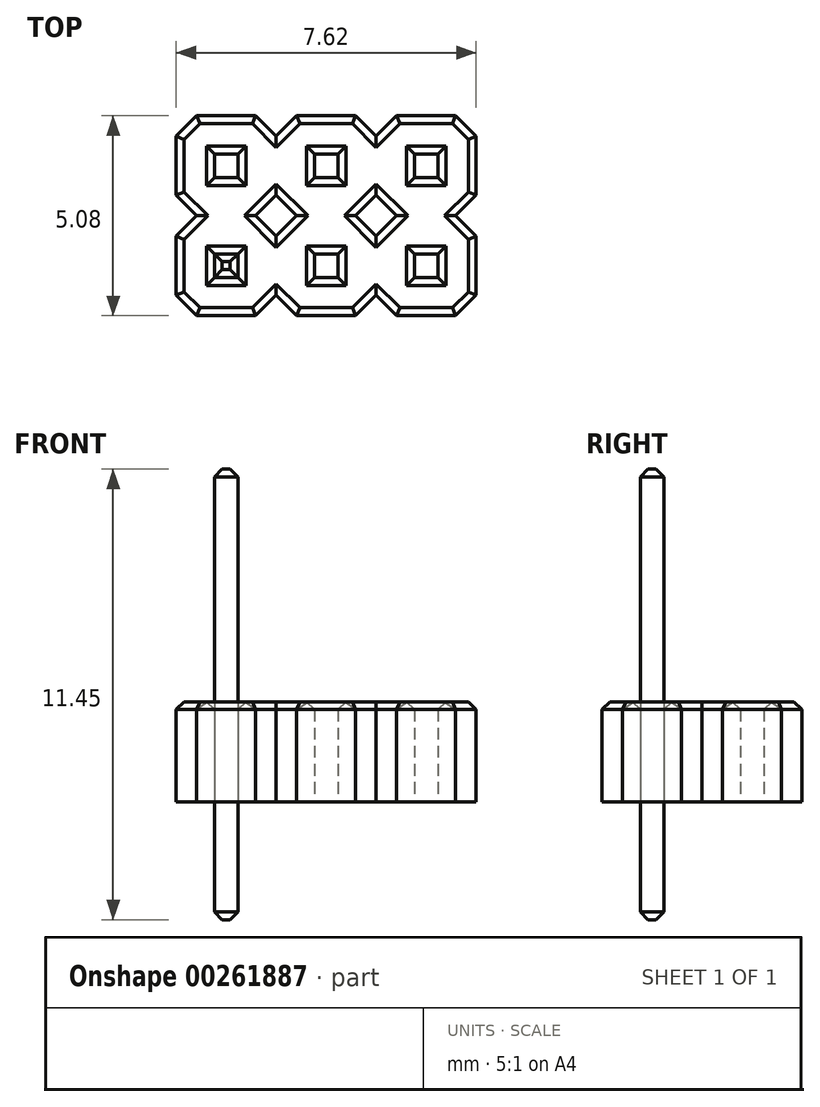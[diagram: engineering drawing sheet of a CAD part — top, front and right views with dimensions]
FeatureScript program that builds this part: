
annotation { "Feature Type Name" : "Feature", "Feature Type Description" : "" }
export const myFeature = defineFeature(function(context is Context, id is Id, definition is map)
    precondition{}
    {
        {
            var Q0;
            Q0=qCreatedBy(makeId("Top.planeOp"),FACE);
            var sketch = newSketch(context, id + "F0", { "sketchPlane" : qUnion([Q0])});
            skLineSegment(sketch, "E0.bottom", {"start": v(0.3, -0.3) * mm, "end": v(-0.3, -0.3) * mm});
            skLineSegment(sketch, "E0.top", {"start": v(0.3, 0.3) * mm, "end": v(-0.3, 0.3) * mm});
            skLineSegment(sketch, "E0.left", {"start": v(0.3, -0.3) * mm, "end": v(0.3, 0.3) * mm});
            skLineSegment(sketch, "E0.right", {"start": v(-0.3, -0.3) * mm, "end": v(-0.3, 0.3) * mm});
            skPoint(sketch, "E0.middle", {"position": v(0, 0) * mm});
            skLineSegment(sketch, "E1.0.1.0", {"start": v(0.3, 2.84) * mm, "end": v(-0.3, 2.84) * mm});
            skLineSegment(sketch, "E1.0.1.1", {"start": v(-0.3, 2.24) * mm, "end": v(-0.3, 2.84) * mm});
            skLineSegment(sketch, "E1.0.1.2", {"start": v(0.3, 2.24) * mm, "end": v(-0.3, 2.24) * mm});
            skLineSegment(sketch, "E1.0.1.3", {"start": v(0.3, 2.24) * mm, "end": v(0.3, 2.84) * mm});
            skLineSegment(sketch, "E1.1.0.0", {"start": v(2.84, 0.3) * mm, "end": v(2.24, 0.3) * mm});
            skLineSegment(sketch, "E1.1.0.1", {"start": v(2.24, -0.3) * mm, "end": v(2.24, 0.3) * mm});
            skLineSegment(sketch, "E1.1.0.2", {"start": v(2.84, -0.3) * mm, "end": v(2.24, -0.3) * mm});
            skLineSegment(sketch, "E1.1.0.3", {"start": v(2.84, -0.3) * mm, "end": v(2.84, 0.3) * mm});
            skLineSegment(sketch, "E1.1.1.0", {"start": v(2.84, 2.84) * mm, "end": v(2.24, 2.84) * mm});
            skLineSegment(sketch, "E1.1.1.1", {"start": v(2.24, 2.24) * mm, "end": v(2.24, 2.84) * mm});
            skLineSegment(sketch, "E1.1.1.2", {"start": v(2.84, 2.24) * mm, "end": v(2.24, 2.24) * mm});
            skLineSegment(sketch, "E1.1.1.3", {"start": v(2.84, 2.24) * mm, "end": v(2.84, 2.84) * mm});
            skLineSegment(sketch, "E1.2.0.0", {"start": v(5.38, 0.3) * mm, "end": v(4.78, 0.3) * mm});
            skLineSegment(sketch, "E1.2.0.1", {"start": v(4.78, -0.3) * mm, "end": v(4.78, 0.3) * mm});
            skLineSegment(sketch, "E1.2.0.2", {"start": v(5.38, -0.3) * mm, "end": v(4.78, -0.3) * mm});
            skLineSegment(sketch, "E1.2.0.3", {"start": v(5.38, -0.3) * mm, "end": v(5.38, 0.3) * mm});
            skLineSegment(sketch, "E1.2.1.0", {"start": v(5.38, 2.84) * mm, "end": v(4.78, 2.84) * mm});
            skLineSegment(sketch, "E1.2.1.1", {"start": v(4.78, 2.24) * mm, "end": v(4.78, 2.84) * mm});
            skLineSegment(sketch, "E1.2.1.2", {"start": v(5.38, 2.24) * mm, "end": v(4.78, 2.24) * mm});
            skLineSegment(sketch, "E1.2.1.3", {"start": v(5.38, 2.24) * mm, "end": v(5.38, 2.84) * mm});
            skLineSegment(sketch, "E1.direction1", {"start": v(-0.3, 0.3) * mm, "end": v(2.24, 0.3) * mm, "construction": true});
            skLineSegment(sketch, "E1.direction2", {"start": v(-0.3, 0.3) * mm, "end": v(-0.3, 2.84) * mm, "construction": true});
            skSolve(sketch);
        }
        {
            var Q0;
            Q0=qCreatedBy(makeId("Top.planeOp"),FACE);
            cPlane(context, id + "F1", {"entities" : qUnion([Q0]), "cplaneType" : CPlaneType.OFFSET, "offset" : 3 * mm, "width" : 150 * mm, "height" : 150 * mm});
        }
        {
            var Q0;
            Q0=qCreatedBy(id+"F1.planeOp",FACE);
            var sketch = newSketch(context, id + "F2", { "sketchPlane" : qUnion([Q0])});
            skLineSegment(sketch, "E2.bottom", {"start": v(0.75, 1.27) * mm, "end": v(-0.75, 1.27) * mm});
            skLineSegment(sketch, "E2.top", {"start": v(0.75, -1.27) * mm, "end": v(-0.75, -1.27) * mm});
            skLineSegment(sketch, "E2.left", {"start": v(1.27, 0.75) * mm, "end": v(1.27, -0.75) * mm});
            skLineSegment(sketch, "E2.right", {"start": v(-1.27, 0.75) * mm, "end": v(-1.27, -0.75) * mm});
            skPoint(sketch, "E2.middle", {"position": v(0, 0) * mm});
            skLineSegment(sketch, "E3", {"start": v(-1.27, 0.75) * mm, "end": v(-0.75, 1.27) * mm});
            skLineSegment(sketch, "E4", {"start": v(1.27, 0.75) * mm, "end": v(0.75, 1.27) * mm});
            skLineSegment(sketch, "E5", {"start": v(-1.27, -0.75) * mm, "end": v(-0.75, -1.27) * mm});
            skLineSegment(sketch, "E6", {"start": v(0.75, -1.27) * mm, "end": v(1.27, -0.75) * mm});
            skPoint(sketch, "E7.orphan", {"position": v(1.27, 1.27) * mm});
            skPoint(sketch, "E8.orphan", {"position": v(-1.27, 1.27) * mm});
            skPoint(sketch, "E9.orphan", {"position": v(-1.27, -1.27) * mm});
            skPoint(sketch, "E10.orphan", {"position": v(1.27, -1.27) * mm});
            skLineSegment(sketch, "E11.0.1.1", {"start": v(0.75, 1.27) * mm, "end": v(1.27, 1.8) * mm});
            skLineSegment(sketch, "E11.0.1.2", {"start": v(1.27, 3.29) * mm, "end": v(1.27, 1.8) * mm});
            skLineSegment(sketch, "E11.0.1.3", {"start": v(1.27, 3.29) * mm, "end": v(0.75, 3.8) * mm});
            skLineSegment(sketch, "E11.0.1.4", {"start": v(0.75, 3.81) * mm, "end": v(-0.75, 3.81) * mm});
            skLineSegment(sketch, "E11.0.1.5", {"start": v(-1.27, 3.29) * mm, "end": v(-0.75, 3.8) * mm});
            skLineSegment(sketch, "E11.0.1.6", {"start": v(-1.27, 3.29) * mm, "end": v(-1.27, 1.8) * mm});
            skLineSegment(sketch, "E11.0.1.7", {"start": v(-1.27, 1.8) * mm, "end": v(-0.75, 1.27) * mm});
            skLineSegment(sketch, "E11.1.0.0", {"start": v(3.29, -1.27) * mm, "end": v(1.8, -1.27) * mm});
            skLineSegment(sketch, "E11.1.0.1", {"start": v(3.29, -1.27) * mm, "end": v(3.8, -0.75) * mm});
            skLineSegment(sketch, "E11.1.0.2", {"start": v(3.81, 0.75) * mm, "end": v(3.81, -0.75) * mm});
            skLineSegment(sketch, "E11.1.0.3", {"start": v(3.81, 0.75) * mm, "end": v(3.29, 1.27) * mm});
            skLineSegment(sketch, "E11.1.0.4", {"start": v(3.29, 1.27) * mm, "end": v(1.8, 1.27) * mm});
            skLineSegment(sketch, "E11.1.0.5", {"start": v(1.27, 0.75) * mm, "end": v(1.8, 1.27) * mm});
            skLineSegment(sketch, "E11.1.0.7", {"start": v(1.27, -0.75) * mm, "end": v(1.8, -1.27) * mm});
            skLineSegment(sketch, "E11.1.1.0", {"start": v(3.29, 1.27) * mm, "end": v(1.8, 1.27) * mm});
            skLineSegment(sketch, "E11.1.1.1", {"start": v(3.29, 1.27) * mm, "end": v(3.8, 1.8) * mm});
            skLineSegment(sketch, "E11.1.1.2", {"start": v(3.81, 3.29) * mm, "end": v(3.81, 1.8) * mm});
            skLineSegment(sketch, "E11.1.1.3", {"start": v(3.81, 3.29) * mm, "end": v(3.29, 3.8) * mm});
            skLineSegment(sketch, "E11.1.1.4", {"start": v(3.29, 3.81) * mm, "end": v(1.8, 3.81) * mm});
            skLineSegment(sketch, "E11.1.1.5", {"start": v(1.27, 3.29) * mm, "end": v(1.8, 3.8) * mm});
            skLineSegment(sketch, "E11.1.1.6", {"start": v(1.27, 3.29) * mm, "end": v(1.27, 1.8) * mm});
            skLineSegment(sketch, "E11.1.1.7", {"start": v(1.27, 1.8) * mm, "end": v(1.8, 1.27) * mm});
            skLineSegment(sketch, "E11.2.0.0", {"start": v(5.83, -1.27) * mm, "end": v(4.33, -1.27) * mm});
            skLineSegment(sketch, "E11.2.0.1", {"start": v(5.83, -1.27) * mm, "end": v(6.35, -0.75) * mm});
            skLineSegment(sketch, "E11.2.0.2", {"start": v(6.35, 0.75) * mm, "end": v(6.35, -0.75) * mm});
            skLineSegment(sketch, "E11.2.0.3", {"start": v(6.35, 0.75) * mm, "end": v(5.83, 1.27) * mm});
            skLineSegment(sketch, "E11.2.0.4", {"start": v(5.83, 1.27) * mm, "end": v(4.33, 1.27) * mm});
            skLineSegment(sketch, "E11.2.0.5", {"start": v(3.8, 0.75) * mm, "end": v(4.33, 1.27) * mm});
            skLineSegment(sketch, "E11.2.0.6", {"start": v(3.81, 0.75) * mm, "end": v(3.81, -0.75) * mm});
            skLineSegment(sketch, "E11.2.0.7", {"start": v(3.8, -0.75) * mm, "end": v(4.33, -1.27) * mm});
            skLineSegment(sketch, "E11.2.1.0", {"start": v(5.83, 1.27) * mm, "end": v(4.33, 1.27) * mm});
            skLineSegment(sketch, "E11.2.1.1", {"start": v(5.83, 1.27) * mm, "end": v(6.35, 1.8) * mm});
            skLineSegment(sketch, "E11.2.1.2", {"start": v(6.35, 3.29) * mm, "end": v(6.35, 1.8) * mm});
            skLineSegment(sketch, "E11.2.1.3", {"start": v(6.35, 3.29) * mm, "end": v(5.83, 3.8) * mm});
            skLineSegment(sketch, "E11.2.1.4", {"start": v(5.83, 3.81) * mm, "end": v(4.33, 3.81) * mm});
            skLineSegment(sketch, "E11.2.1.5", {"start": v(3.8, 3.29) * mm, "end": v(4.33, 3.8) * mm});
            skLineSegment(sketch, "E11.2.1.6", {"start": v(3.81, 3.29) * mm, "end": v(3.81, 1.8) * mm});
            skLineSegment(sketch, "E11.2.1.7", {"start": v(3.8, 1.8) * mm, "end": v(4.33, 1.27) * mm});
            skLineSegment(sketch, "E11.direction1", {"start": v(-0.75, -1.27) * mm, "end": v(1.8, -1.27) * mm, "construction": true});
            skLineSegment(sketch, "E11.direction2", {"start": v(-0.75, -1.27) * mm, "end": v(-0.75, 1.27) * mm, "construction": true});
            skLineSegment(sketch, "E12.bottom", {"start": v(0.3, -0.3) * mm, "end": v(-0.3, -0.3) * mm});
            skLineSegment(sketch, "E12.top", {"start": v(0.3, 0.3) * mm, "end": v(-0.3, 0.3) * mm});
            skLineSegment(sketch, "E12.left", {"start": v(0.3, -0.3) * mm, "end": v(0.3, 0.3) * mm});
            skLineSegment(sketch, "E12.right", {"start": v(-0.3, -0.3) * mm, "end": v(-0.3, 0.3) * mm});
            skLineSegment(sketch, "E13.0.1.0", {"start": v(0.3, 2.84) * mm, "end": v(-0.3, 2.84) * mm});
            skLineSegment(sketch, "E13.0.1.1", {"start": v(0.3, 2.24) * mm, "end": v(0.3, 2.84) * mm});
            skLineSegment(sketch, "E13.0.1.2", {"start": v(0.3, 2.24) * mm, "end": v(-0.3, 2.24) * mm});
            skLineSegment(sketch, "E13.0.1.3", {"start": v(-0.3, 2.24) * mm, "end": v(-0.3, 2.84) * mm});
            skLineSegment(sketch, "E13.1.0.0", {"start": v(2.84, 0.3) * mm, "end": v(2.24, 0.3) * mm});
            skLineSegment(sketch, "E13.1.0.1", {"start": v(2.84, -0.3) * mm, "end": v(2.84, 0.3) * mm});
            skLineSegment(sketch, "E13.1.0.2", {"start": v(2.84, -0.3) * mm, "end": v(2.24, -0.3) * mm});
            skLineSegment(sketch, "E13.1.0.3", {"start": v(2.24, -0.3) * mm, "end": v(2.24, 0.3) * mm});
            skLineSegment(sketch, "E13.1.1.0", {"start": v(2.84, 2.84) * mm, "end": v(2.24, 2.84) * mm});
            skLineSegment(sketch, "E13.1.1.1", {"start": v(2.84, 2.24) * mm, "end": v(2.84, 2.84) * mm});
            skLineSegment(sketch, "E13.1.1.2", {"start": v(2.84, 2.24) * mm, "end": v(2.24, 2.24) * mm});
            skLineSegment(sketch, "E13.1.1.3", {"start": v(2.24, 2.24) * mm, "end": v(2.24, 2.84) * mm});
            skLineSegment(sketch, "E13.2.0.0", {"start": v(5.38, 0.3) * mm, "end": v(4.78, 0.3) * mm});
            skLineSegment(sketch, "E13.2.0.1", {"start": v(5.38, -0.3) * mm, "end": v(5.38, 0.3) * mm});
            skLineSegment(sketch, "E13.2.0.2", {"start": v(5.38, -0.3) * mm, "end": v(4.78, -0.3) * mm});
            skLineSegment(sketch, "E13.2.0.3", {"start": v(4.78, -0.3) * mm, "end": v(4.78, 0.3) * mm});
            skLineSegment(sketch, "E13.2.1.0", {"start": v(5.38, 2.84) * mm, "end": v(4.78, 2.84) * mm});
            skLineSegment(sketch, "E13.2.1.1", {"start": v(5.38, 2.24) * mm, "end": v(5.38, 2.84) * mm});
            skLineSegment(sketch, "E13.2.1.2", {"start": v(5.38, 2.24) * mm, "end": v(4.78, 2.24) * mm});
            skLineSegment(sketch, "E13.2.1.3", {"start": v(4.78, 2.24) * mm, "end": v(4.78, 2.84) * mm});
            skLineSegment(sketch, "E13.direction1", {"start": v(-0.3, 0.3) * mm, "end": v(2.24, 0.3) * mm, "construction": true});
            skLineSegment(sketch, "E13.direction2", {"start": v(-0.3, 0.3) * mm, "end": v(-0.3, 2.84) * mm, "construction": true});
            skSolve(sketch);
        }
        {
            var Q0;
            Q0 = qSketchRegion(id + "F2", true);
            extrude(context, id + "F3", {"entities" : qUnion([Q0]), "depth" : 2.54 * mm});
        }
        {
            var Q0;
            Q0 = qSketchRegion(id + "F0", true);
            extrude(context, id + "F4", {"entities" : qUnion([Q0]), "depth" : 11.45 * mm});
        }
        {
            var Q0;
            Q0=makeQuery(id+"F4.opExtrude","CAP_FACE",FACE,{"disambiguationData":[OSD([sQuery(id+"F0.wireOp",EDGE,"E1.0.1.0"),sQuery(id+"F0.wireOp",EDGE,"E1.0.1.1"),sQuery(id+"F0.wireOp",EDGE,"E1.0.1.2"),sQuery(id+"F0.wireOp",EDGE,"E1.0.1.3")])],"isStart":false});
            var Q1;
            Q1=makeQuery(id+"F4.opExtrude","CAP_FACE",FACE,{"disambiguationData":[OSD([sQuery(id+"F0.wireOp",EDGE,"E0.bottom"),sQuery(id+"F0.wireOp",EDGE,"E0.top"),sQuery(id+"F0.wireOp",EDGE,"E0.left"),sQuery(id+"F0.wireOp",EDGE,"E0.right")])],"isStart":false});
            var Q2;
            Q2=makeQuery(id+"F4.opExtrude","CAP_FACE",FACE,{"disambiguationData":[OSD([sQuery(id+"F0.wireOp",EDGE,"E1.1.1.0"),sQuery(id+"F0.wireOp",EDGE,"E1.1.1.1"),sQuery(id+"F0.wireOp",EDGE,"E1.1.1.2"),sQuery(id+"F0.wireOp",EDGE,"E1.1.1.3")])],"isStart":false});
            var Q3;
            Q3=makeQuery(id+"F4.opExtrude","CAP_FACE",FACE,{"disambiguationData":[OSD([sQuery(id+"F0.wireOp",EDGE,"E1.1.0.0"),sQuery(id+"F0.wireOp",EDGE,"E1.1.0.1"),sQuery(id+"F0.wireOp",EDGE,"E1.1.0.2"),sQuery(id+"F0.wireOp",EDGE,"E1.1.0.3")])],"isStart":false});
            var Q4;
            Q4=makeQuery(id+"F4.opExtrude","CAP_FACE",FACE,{"disambiguationData":[OSD([sQuery(id+"F0.wireOp",EDGE,"E1.2.0.0"),sQuery(id+"F0.wireOp",EDGE,"E1.2.0.1"),sQuery(id+"F0.wireOp",EDGE,"E1.2.0.2"),sQuery(id+"F0.wireOp",EDGE,"E1.2.0.3")])],"isStart":false});
            var Q5;
            Q5=makeQuery(id+"F4.opExtrude","CAP_FACE",FACE,{"disambiguationData":[OSD([sQuery(id+"F0.wireOp",EDGE,"E1.2.1.0"),sQuery(id+"F0.wireOp",EDGE,"E1.2.1.1"),sQuery(id+"F0.wireOp",EDGE,"E1.2.1.2"),sQuery(id+"F0.wireOp",EDGE,"E1.2.1.3")])],"isStart":false});
            var Q6;
            Q6=makeQuery(id+"F4.opExtrude","CAP_FACE",FACE,{"disambiguationData":[OSD([sQuery(id+"F0.wireOp",EDGE,"E0.bottom"),sQuery(id+"F0.wireOp",EDGE,"E0.top"),sQuery(id+"F0.wireOp",EDGE,"E0.left"),sQuery(id+"F0.wireOp",EDGE,"E0.right")])],"isStart":true});
            var Q7;
            Q7=makeQuery(id+"F4.opExtrude","CAP_FACE",FACE,{"disambiguationData":[OSD([sQuery(id+"F0.wireOp",EDGE,"E1.0.1.0"),sQuery(id+"F0.wireOp",EDGE,"E1.0.1.1"),sQuery(id+"F0.wireOp",EDGE,"E1.0.1.2"),sQuery(id+"F0.wireOp",EDGE,"E1.0.1.3")])],"isStart":true});
            var Q8;
            Q8=makeQuery(id+"F4.opExtrude","CAP_FACE",FACE,{"disambiguationData":[OSD([sQuery(id+"F0.wireOp",EDGE,"E1.1.1.0"),sQuery(id+"F0.wireOp",EDGE,"E1.1.1.1"),sQuery(id+"F0.wireOp",EDGE,"E1.1.1.2"),sQuery(id+"F0.wireOp",EDGE,"E1.1.1.3")])],"isStart":true});
            var Q9;
            Q9=makeQuery(id+"F4.opExtrude","CAP_FACE",FACE,{"disambiguationData":[OSD([sQuery(id+"F0.wireOp",EDGE,"E1.1.0.0"),sQuery(id+"F0.wireOp",EDGE,"E1.1.0.1"),sQuery(id+"F0.wireOp",EDGE,"E1.1.0.2"),sQuery(id+"F0.wireOp",EDGE,"E1.1.0.3")])],"isStart":true});
            var Q10;
            Q10=makeQuery(id+"F4.opExtrude","CAP_FACE",FACE,{"disambiguationData":[OSD([sQuery(id+"F0.wireOp",EDGE,"E1.2.0.0"),sQuery(id+"F0.wireOp",EDGE,"E1.2.0.1"),sQuery(id+"F0.wireOp",EDGE,"E1.2.0.2"),sQuery(id+"F0.wireOp",EDGE,"E1.2.0.3")])],"isStart":true});
            var Q11;
            Q11=makeQuery(id+"F4.opExtrude","CAP_FACE",FACE,{"disambiguationData":[OSD([sQuery(id+"F0.wireOp",EDGE,"E1.2.1.0"),sQuery(id+"F0.wireOp",EDGE,"E1.2.1.1"),sQuery(id+"F0.wireOp",EDGE,"E1.2.1.2"),sQuery(id+"F0.wireOp",EDGE,"E1.2.1.3")])],"isStart":true});
            chamfer(context, id + "F5", {"entities" : qUnion([Q0, Q1, Q2, Q3, Q4, Q5, Q6, Q7, Q8, Q9, Q10, Q11]), "width" : 0.2 * mm, "tangentPropagation" : true});
        }
        {
            var Q0;
            Q0=makeQuery(id+"F3.opExtrude","CAP_FACE",FACE,{"disambiguationData":[OSD([sQuery(id+"F2.wireOp",EDGE,"E2.top"),sQuery(id+"F2.wireOp",EDGE,"E2.right"),sQuery(id+"F2.wireOp",EDGE,"E3"),sQuery(id+"F2.wireOp",EDGE,"E4"),sQuery(id+"F2.wireOp",EDGE,"E5"),sQuery(id+"F2.wireOp",EDGE,"E6"),sQuery(id+"F2.wireOp",EDGE,"E11.0.1.1"),sQuery(id+"F2.wireOp",EDGE,"E11.0.1.3"),sQuery(id+"F2.wireOp",EDGE,"E11.0.1.4"),sQuery(id+"F2.wireOp",EDGE,"E11.0.1.5"),sQuery(id+"F2.wireOp",EDGE,"E11.0.1.6"),sQuery(id+"F2.wireOp",EDGE,"E11.0.1.7"),sQuery(id+"F2.wireOp",EDGE,"E11.1.0.0"),sQuery(id+"F2.wireOp",EDGE,"E11.1.0.1"),sQuery(id+"F2.wireOp",EDGE,"E11.1.0.3"),sQuery(id+"F2.wireOp",EDGE,"E11.1.0.5"),sQuery(id+"F2.wireOp",EDGE,"E11.1.0.7"),sQuery(id+"F2.wireOp",EDGE,"E11.1.1.1"),sQuery(id+"F2.wireOp",EDGE,"E11.1.1.3"),sQuery(id+"F2.wireOp",EDGE,"E11.1.1.4"),sQuery(id+"F2.wireOp",EDGE,"E11.1.1.5"),sQuery(id+"F2.wireOp",EDGE,"E11.1.1.7"),sQuery(id+"F2.wireOp",EDGE,"E11.2.0.0"),sQuery(id+"F2.wireOp",EDGE,"E11.2.0.1"),sQuery(id+"F2.wireOp",EDGE,"E11.2.0.2"),sQuery(id+"F2.wireOp",EDGE,"E11.2.0.3"),sQuery(id+"F2.wireOp",EDGE,"E11.2.0.5"),sQuery(id+"F2.wireOp",EDGE,"E11.2.0.7"),sQuery(id+"F2.wireOp",EDGE,"E11.2.1.1"),sQuery(id+"F2.wireOp",EDGE,"E11.2.1.2"),sQuery(id+"F2.wireOp",EDGE,"E11.2.1.3"),sQuery(id+"F2.wireOp",EDGE,"E11.2.1.4"),sQuery(id+"F2.wireOp",EDGE,"E11.2.1.5"),sQuery(id+"F2.wireOp",EDGE,"E11.2.1.7")])],"isStart":false});
            chamfer(context, id + "F6", {"entities" : qUnion([Q0]), "width" : 0.2 * mm, "tangentPropagation" : true});
        }
        {
            var Q0;
            Q0=makeQuery(id+"F4.opExtrude","SWEPT_BODY",BODY,{"disambiguationData":[OSD([sQuery(id+"F0.wireOp",EDGE,"E1.2.1.0"),sQuery(id+"F0.wireOp",EDGE,"E1.2.1.1"),sQuery(id+"F0.wireOp",EDGE,"E1.2.1.2"),sQuery(id+"F0.wireOp",EDGE,"E1.2.1.3")])]});
            var Q1;
            Q1=makeQuery(id+"F4.opExtrude","SWEPT_BODY",BODY,{"disambiguationData":[OSD([sQuery(id+"F0.wireOp",EDGE,"E1.2.0.0"),sQuery(id+"F0.wireOp",EDGE,"E1.2.0.1"),sQuery(id+"F0.wireOp",EDGE,"E1.2.0.2"),sQuery(id+"F0.wireOp",EDGE,"E1.2.0.3")])]});
            var Q2;
            Q2=makeQuery(id+"F4.opExtrude","SWEPT_BODY",BODY,{"disambiguationData":[OSD([sQuery(id+"F0.wireOp",EDGE,"E1.1.1.0"),sQuery(id+"F0.wireOp",EDGE,"E1.1.1.1"),sQuery(id+"F0.wireOp",EDGE,"E1.1.1.2"),sQuery(id+"F0.wireOp",EDGE,"E1.1.1.3")])]});
            var Q3;
            Q3=makeQuery(id+"F4.opExtrude","SWEPT_BODY",BODY,{"disambiguationData":[OSD([sQuery(id+"F0.wireOp",EDGE,"E1.1.0.0"),sQuery(id+"F0.wireOp",EDGE,"E1.1.0.1"),sQuery(id+"F0.wireOp",EDGE,"E1.1.0.2"),sQuery(id+"F0.wireOp",EDGE,"E1.1.0.3")])]});
            var Q4;
            Q4=makeQuery(id+"F4.opExtrude","SWEPT_BODY",BODY,{"disambiguationData":[OSD([sQuery(id+"F0.wireOp",EDGE,"E1.0.1.0"),sQuery(id+"F0.wireOp",EDGE,"E1.0.1.1"),sQuery(id+"F0.wireOp",EDGE,"E1.0.1.2"),sQuery(id+"F0.wireOp",EDGE,"E1.0.1.3")])]});
            deleteBodies(context, id + "F7", {"entities" : qUnion([Q0, Q1, Q2, Q3, Q4])});
        }
    });
